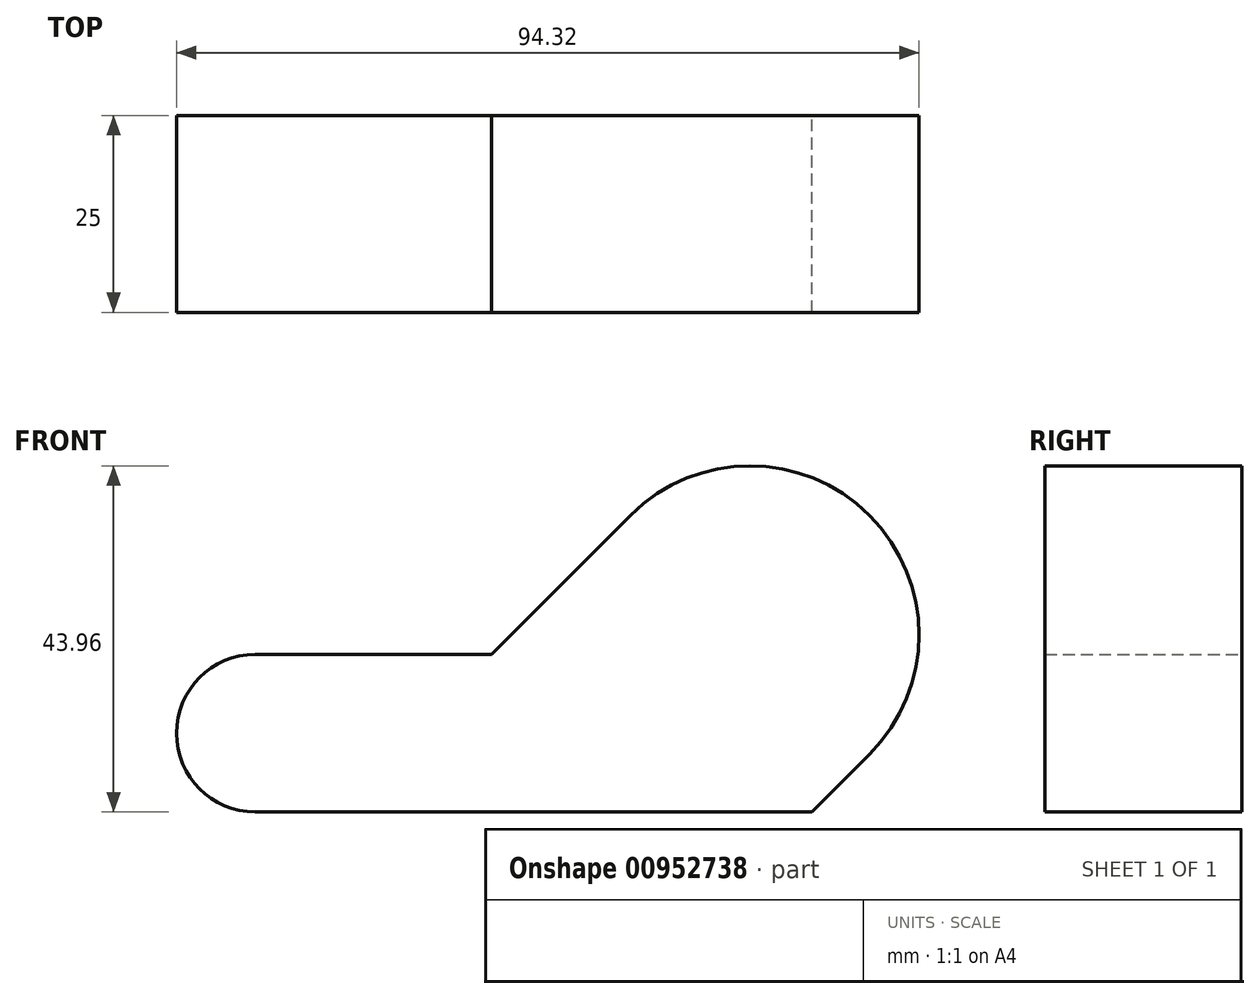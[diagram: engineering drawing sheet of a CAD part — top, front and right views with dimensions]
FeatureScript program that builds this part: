
annotation { "Feature Type Name" : "Feature", "Feature Type Description" : "" }
export const myFeature = defineFeature(function(context is Context, id is Id, definition is map)
    precondition{}
    {
        {
            var Q0;
            Q0=qCreatedBy(makeId("Front.planeOp"),FACE);
            var sketch = newSketch(context, id + "F0", { "sketchPlane" : qUnion([Q0])});
            skLineSegment(sketch, "E0", {"start": v(0, 0) * mm, "end": v(70.71, 0) * mm});
            skLineSegment(sketch, "E1", {"start": v(70.71, 0) * mm, "end": v(78.03, 7.32) * mm});
            skLineSegment(sketch, "E2", {"start": v(78.03, 7.32) * mm, "end": v(47.68, 37.68) * mm});
            skLineSegment(sketch, "E3", {"start": v(47.68, 37.68) * mm, "end": v(30, 20) * mm});
            skLineSegment(sketch, "E4", {"start": v(30, 20) * mm, "end": v(0, 20) * mm});
            skLineSegment(sketch, "E5", {"start": v(0, 20) * mm, "end": v(0, 0) * mm});
            skArc(sketch, "E6", {"start": v(47.68, 37.68) * mm, "mid": v(78.03, 37.68) * mm, "end": v(78.03, 7.32) * mm});
            skArc(sketch, "E7", {"start": v(0, 0) * mm, "mid": v(-10, 10) * mm, "end": v(0, 20) * mm});
            skSolve(sketch);
        }
        {
            var Q0;
            Q0=makeQuery(id+"F0.imprint","IMPRINT",FACE,{"disambiguationData":[TD([[makeQuery(id+"F0.imprint","IMPRINT",EDGE,{"derivedFrom":sQuery(id+"F0.wireOp",EDGE,"E5")}),-1.0]])]});
            var Q1;
            Q1=makeQuery(id+"F0.imprint","IMPRINT",FACE,{"disambiguationData":[TD([[makeQuery(id+"F0.imprint","IMPRINT",EDGE,{"derivedFrom":sQuery(id+"F0.wireOp",EDGE,"E0")}),1.0]])]});
            var Q2;
            Q2=makeQuery(id+"F0.imprint","IMPRINT",FACE,{"disambiguationData":[TD([[makeQuery(id+"F0.imprint","IMPRINT",EDGE,{"derivedFrom":sQuery(id+"F0.wireOp",EDGE,"E2")}),-1.0]])]});
            extrude(context, id + "F1", {"entities" : qUnion([Q0, Q1, Q2]), "depth" : 25 * mm, "offsetDistance" : 25 * mm});
        }
    });
